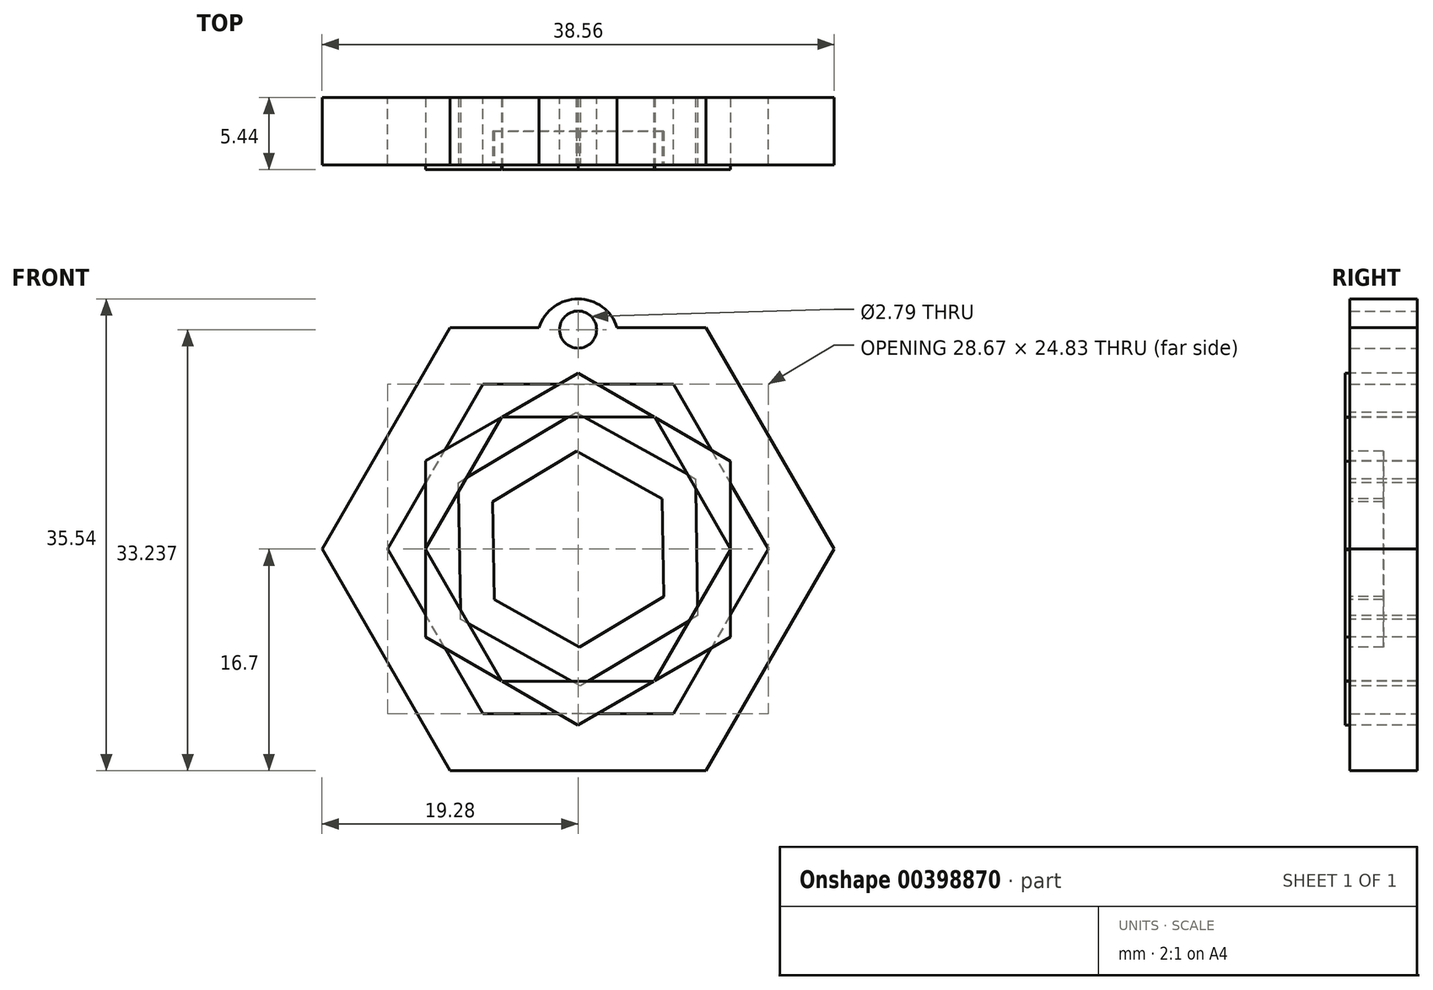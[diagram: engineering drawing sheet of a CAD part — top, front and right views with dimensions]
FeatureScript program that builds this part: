
annotation { "Feature Type Name" : "Feature", "Feature Type Description" : "" }
export const myFeature = defineFeature(function(context is Context, id is Id, definition is map)
    precondition{}
    {
        {
            var Q0;
            Q0=qCreatedBy(makeId("Front.planeOp"),FACE);
            var sketch = newSketch(context, id + "F0", { "sketchPlane" : qUnion([Q0])});
            skCircle(sketch, "E0.cCircle", {"center": v(0, 0) * mm, "radius": 16.7 * mm, "construction": true});
            skLineSegment(sketch, "E0.0", {"start": v(9.64, -16.7) * mm, "end": v(-9.64, -16.7) * mm});
            skLineSegment(sketch, "E0.1", {"start": v(-9.64, -16.7) * mm, "end": v(-19.28, 0) * mm});
            skLineSegment(sketch, "E0.2", {"start": v(-19.28, 0) * mm, "end": v(-9.64, 16.7) * mm});
            skLineSegment(sketch, "E0.3", {"start": v(-9.64, 16.7) * mm, "end": v(9.64, 16.7) * mm});
            skLineSegment(sketch, "E0.4", {"start": v(9.64, 16.7) * mm, "end": v(19.28, 0) * mm});
            skLineSegment(sketch, "E0.5", {"start": v(19.28, 0) * mm, "end": v(9.64, -16.7) * mm});
            skPoint(sketch, "E0.0.midPoint", {"position": v(0, -16.7) * mm});
            skCircle(sketch, "E1.cCircle", {"center": v(0, 0) * mm, "radius": 12.42 * mm, "construction": true});
            skLineSegment(sketch, "E1.0", {"start": v(7.17, -12.42) * mm, "end": v(-7.17, -12.42) * mm});
            skLineSegment(sketch, "E1.1", {"start": v(-7.17, -12.42) * mm, "end": v(-14.34, 0) * mm});
            skLineSegment(sketch, "E1.2", {"start": v(-14.34, 0) * mm, "end": v(-7.17, 12.42) * mm});
            skLineSegment(sketch, "E1.3", {"start": v(-7.17, 12.42) * mm, "end": v(7.17, 12.42) * mm});
            skLineSegment(sketch, "E1.4", {"start": v(7.17, 12.42) * mm, "end": v(14.34, 0) * mm});
            skLineSegment(sketch, "E1.5", {"start": v(14.34, 0) * mm, "end": v(7.17, -12.42) * mm});
            skPoint(sketch, "E1.0.midPoint", {"position": v(0, -12.42) * mm});
            skSolve(sketch);
        }
        {
            var Q0;
            Q0=makeQuery(id+"F0.imprint","IMPRINT",FACE,{"disambiguationData":[TD([[makeQuery(id+"F0.imprint","IMPRINT",EDGE,{"derivedFrom":sQuery(id+"F0.wireOp",EDGE,"E0.0")}),-1.0]])]});
            extrude(context, id + "F1", {"entities" : qUnion([Q0]), "depth" : 5.08 * mm});
        }
        {
            var Q0;
            Q0=qCreatedBy(makeId("Front.planeOp"),FACE);
            var sketch = newSketch(context, id + "F2", { "sketchPlane" : qUnion([Q0])});
            skCircle(sketch, "E2", {"center": v(0, 15.77) * mm, "radius": 3.08 * mm});
            skSolve(sketch);
        }
        {
            var Q0;
            Q0=makeQuery(id+"F2.imprint","IMPRINT",FACE,{"disambiguationData":[TD([[makeQuery(id+"F2.imprint","IMPRINT",EDGE,{"derivedFrom":sQuery(id+"F2.wireOp",EDGE,"E2")}),1.0]])]});
            extrude(context, id + "F3", {"entities" : qUnion([Q0]), "operationType" : NewBodyOperationType.ADD, "depth" : 5.08 * mm});
        }
        {
            var Q0;
            Q0=qCreatedBy(makeId("Front.planeOp"),FACE);
            var sketch = newSketch(context, id + "F4", { "sketchPlane" : qUnion([Q0])});
            skPoint(sketch, "E3", {"position": v(0, 16.54) * mm});
            skSolve(sketch);
        }
        {
            var Q0;
            Q0=sQuery(id+"F4.wireOp",VERTEX,"E3");
            var Q1;
            Q1=makeQuery(id+"F1.opExtrude","SWEPT_BODY",BODY,{"disambiguationData":[OSD([sQuery(id+"F0.wireOp",EDGE,"E0.0"),sQuery(id+"F0.wireOp",EDGE,"E0.1"),sQuery(id+"F0.wireOp",EDGE,"E0.2"),sQuery(id+"F0.wireOp",EDGE,"E0.3"),sQuery(id+"F0.wireOp",EDGE,"E0.4"),sQuery(id+"F0.wireOp",EDGE,"E0.5"),sQuery(id+"F0.wireOp",EDGE,"E1.0"),sQuery(id+"F0.wireOp",EDGE,"E1.1"),sQuery(id+"F0.wireOp",EDGE,"E1.2"),sQuery(id+"F0.wireOp",EDGE,"E1.3"),sQuery(id+"F0.wireOp",EDGE,"E1.4"),sQuery(id+"F0.wireOp",EDGE,"E1.5")])]});
            hole(context, id + "F5", {"style" : HoleStyle.SIMPLE, "endStyle" : HoleEndStyle.THROUGH, "oppositeDirection" : true, "holeDiameter" : 2.8 * mm, "isTappedThrough" : true, "tappedDepth" : 12.7 * mm, "tapClearance" : 3, "locations" : qUnion([Q0]), "scope" : qUnion([Q1])});
        }
        {
            var Q0;
            Q0=makeQuery(id+"F3.boolean.opBoolean","MERGE",FACE,{"derivedFrom":[makeQuery(id+"F1.opExtrude","CAP_FACE",FACE,{"disambiguationData":[OSD([sQuery(id+"F0.wireOp",EDGE,"E0.0"),sQuery(id+"F0.wireOp",EDGE,"E0.1"),sQuery(id+"F0.wireOp",EDGE,"E0.2"),sQuery(id+"F0.wireOp",EDGE,"E0.3"),sQuery(id+"F0.wireOp",EDGE,"E0.4"),sQuery(id+"F0.wireOp",EDGE,"E0.5"),sQuery(id+"F0.wireOp",EDGE,"E1.0"),sQuery(id+"F0.wireOp",EDGE,"E1.1"),sQuery(id+"F0.wireOp",EDGE,"E1.2"),sQuery(id+"F0.wireOp",EDGE,"E1.3"),sQuery(id+"F0.wireOp",EDGE,"E1.4"),sQuery(id+"F0.wireOp",EDGE,"E1.5")])],"isStart":false}),makeQuery(id+"F3.opExtrude","CAP_FACE",FACE,{"disambiguationData":[OSD([sQuery(id+"F2.wireOp",EDGE,"E2")])],"isStart":false})]});
            var sketch = newSketch(context, id + "F6", { "sketchPlane" : qUnion([Q0])});
            skCircle(sketch, "E4.cCircle", {"center": v(0, 0) * mm, "radius": 10.73 * mm, "construction": true});
            skLineSegment(sketch, "E4.0", {"start": v(0, 12.39) * mm, "end": v(10.73, 6.19) * mm});
            skLineSegment(sketch, "E4.1", {"start": v(10.73, 6.19) * mm, "end": v(10.72, -6.2) * mm});
            skLineSegment(sketch, "E4.2", {"start": v(10.72, -6.2) * mm, "end": v(0, -12.39) * mm});
            skLineSegment(sketch, "E4.3", {"start": v(0, -12.39) * mm, "end": v(-10.73, -6.19) * mm});
            skLineSegment(sketch, "E4.4", {"start": v(-10.73, -6.19) * mm, "end": v(-10.72, 6.2) * mm});
            skLineSegment(sketch, "E4.5", {"start": v(-10.72, 6.2) * mm, "end": v(0, 12.39) * mm});
            skPoint(sketch, "E4.0.midPoint", {"position": v(5.37, 9.29) * mm});
            skCircle(sketch, "E5.cCircle", {"center": v(0, 0) * mm, "radius": 9.3 * mm, "construction": true});
            skLineSegment(sketch, "E5.0", {"start": v(5.38, 9.3) * mm, "end": v(10.75, 0) * mm});
            skLineSegment(sketch, "E5.1", {"start": v(10.75, 0) * mm, "end": v(5.37, -9.31) * mm});
            skLineSegment(sketch, "E5.2", {"start": v(5.37, -9.31) * mm, "end": v(-5.38, -9.3) * mm});
            skLineSegment(sketch, "E5.3", {"start": v(-5.38, -9.3) * mm, "end": v(-10.75, 0) * mm});
            skLineSegment(sketch, "E5.4", {"start": v(-10.75, 0) * mm, "end": v(-5.37, 9.31) * mm});
            skLineSegment(sketch, "E5.5", {"start": v(-5.37, 9.31) * mm, "end": v(5.38, 9.3) * mm});
            skPoint(sketch, "E5.0.midPoint", {"position": v(8.06, 4.65) * mm});
            skCircle(sketch, "E6.cCircle", {"center": v(0, 0) * mm, "radius": 8.04 * mm, "construction": true});
            skLineSegment(sketch, "E6.0", {"start": v(-8.04, 4.65) * mm, "end": v(0, 9.28) * mm});
            skLineSegment(sketch, "E6.1", {"start": v(0, 9.28) * mm, "end": v(8.04, 4.64) * mm});
            skLineSegment(sketch, "E6.2", {"start": v(8.04, 4.64) * mm, "end": v(8.04, -4.65) * mm});
            skLineSegment(sketch, "E6.3", {"start": v(8.04, -4.65) * mm, "end": v(0, -9.28) * mm});
            skLineSegment(sketch, "E6.4", {"start": v(0, -9.28) * mm, "end": v(-8.04, -4.64) * mm});
            skLineSegment(sketch, "E6.5", {"start": v(-8.04, -4.64) * mm, "end": v(-8.04, 4.65) * mm});
            skPoint(sketch, "E6.0.midPoint", {"position": v(-4.01, 6.97) * mm});
            skCircle(sketch, "E7.cCircle", {"center": v(0, 0) * mm, "radius": 6.97 * mm, "construction": true});
            skLineSegment(sketch, "E7.0", {"start": v(-4.02, 6.97) * mm, "end": v(4.02, 6.97) * mm});
            skLineSegment(sketch, "E7.1", {"start": v(4.02, 6.97) * mm, "end": v(8.04, 0) * mm});
            skLineSegment(sketch, "E7.2", {"start": v(8.04, 0) * mm, "end": v(4.02, -6.97) * mm});
            skLineSegment(sketch, "E7.3", {"start": v(4.02, -6.97) * mm, "end": v(-4.02, -6.97) * mm});
            skLineSegment(sketch, "E7.4", {"start": v(-4.02, -6.97) * mm, "end": v(-8.04, 0) * mm});
            skLineSegment(sketch, "E7.5", {"start": v(-8.04, 0) * mm, "end": v(-4.02, 6.97) * mm});
            skPoint(sketch, "E7.0.midPoint", {"position": v(0, 6.97) * mm});
            skSolve(sketch);
        }
        {
            var Q0;
            {var subQ0=sQuery(id+"F6.wireOp",EDGE,"E4.5");var subQ1=sQuery(id+"F6.wireOp",EDGE,"E4.0");var subQ2=makeQuery(id+"F6.imprint","INTERSECT",VERTEX,{"derivedFrom":[subQ1,subQ0]});Q0=makeQuery(id+"F6.imprint","IMPRINT",FACE,{"disambiguationData":[TD([[makeQuery(id+"F6.imprint","IMPRINT",EDGE,{"disambiguationData":[TD([[subQ2,-1.0]])],"derivedFrom":subQ1}),-1.0]])]});}
            var Q1;
            {var subQ0=sQuery(id+"F6.wireOp",EDGE,"E4.5");var subQ1=sQuery(id+"F6.wireOp",EDGE,"E4.4");var subQ2=makeQuery(id+"F6.imprint","INTERSECT",VERTEX,{"derivedFrom":[subQ1,subQ0]});Q1=makeQuery(id+"F6.imprint","IMPRINT",FACE,{"disambiguationData":[TD([[makeQuery(id+"F6.imprint","IMPRINT",EDGE,{"disambiguationData":[TD([[subQ2,1.0]])],"derivedFrom":subQ1}),-1.0]])]});}
            var Q2;
            {var subQ0=sQuery(id+"F6.wireOp",EDGE,"E4.4");var subQ1=sQuery(id+"F6.wireOp",EDGE,"E4.3");var subQ2=makeQuery(id+"F6.imprint","INTERSECT",VERTEX,{"derivedFrom":[subQ1,subQ0]});Q2=makeQuery(id+"F6.imprint","IMPRINT",FACE,{"disambiguationData":[TD([[makeQuery(id+"F6.imprint","IMPRINT",EDGE,{"disambiguationData":[TD([[subQ2,1.0]])],"derivedFrom":subQ1}),-1.0]])]});}
            var Q3;
            {var subQ14=sQuery(id+"F6.wireOp",EDGE,"E6.0");var subQ20=sQuery(id+"F6.wireOp",EDGE,"E7.5");var subQ23=makeQuery(id+"F6.imprint","INTERSECT",VERTEX,{"derivedFrom":[subQ14,subQ20]});Q3=makeQuery(id+"F6.imprint","IMPRINT",FACE,{"disambiguationData":[TD([[makeQuery(id+"F6.imprint","IMPRINT",EDGE,{"disambiguationData":[TD([[subQ23,-1.0]])],"derivedFrom":subQ14}),-1.0]])]});}
            var Q4;
            {var subQ0=sQuery(id+"F6.wireOp",EDGE,"E4.1");var subQ1=sQuery(id+"F6.wireOp",EDGE,"E4.0");var subQ2=makeQuery(id+"F6.imprint","INTERSECT",VERTEX,{"derivedFrom":[subQ1,subQ0]});Q4=makeQuery(id+"F6.imprint","IMPRINT",FACE,{"disambiguationData":[TD([[makeQuery(id+"F6.imprint","IMPRINT",EDGE,{"disambiguationData":[TD([[subQ2,1.0]])],"derivedFrom":subQ1}),-1.0]])]});}
            var Q5;
            {var subQ0=sQuery(id+"F6.wireOp",EDGE,"E4.2");var subQ1=sQuery(id+"F6.wireOp",EDGE,"E4.1");var subQ2=makeQuery(id+"F6.imprint","INTERSECT",VERTEX,{"derivedFrom":[subQ1,subQ0]});Q5=makeQuery(id+"F6.imprint","IMPRINT",FACE,{"disambiguationData":[TD([[makeQuery(id+"F6.imprint","IMPRINT",EDGE,{"disambiguationData":[TD([[subQ2,1.0]])],"derivedFrom":subQ1}),-1.0]])]});}
            var Q6;
            {var subQ0=sQuery(id+"F6.wireOp",EDGE,"E4.3");var subQ1=sQuery(id+"F6.wireOp",EDGE,"E4.2");var subQ2=makeQuery(id+"F6.imprint","INTERSECT",VERTEX,{"derivedFrom":[subQ1,subQ0]});Q6=makeQuery(id+"F6.imprint","IMPRINT",FACE,{"disambiguationData":[TD([[makeQuery(id+"F6.imprint","IMPRINT",EDGE,{"disambiguationData":[TD([[subQ2,1.0]])],"derivedFrom":subQ1}),-1.0]])]});}
            extrude(context, id + "F7", {"entities" : qUnion([Q0, Q1, Q2, Q3, Q4, Q5, Q6]), "oppositeDirection" : true, "depth" : 5.08 * mm});
        }
        {
            var Q0;
            Q0=makeQuery(id+"F7.opExtrude","SWEPT_BODY",BODY,{"disambiguationData":[OSD([sQuery(id+"F6.wireOp",EDGE,"E4.0"),sQuery(id+"F6.wireOp",EDGE,"E4.1"),sQuery(id+"F6.wireOp",EDGE,"E5.0")])]});
            var Q1;
            Q1=makeQuery(id+"F7.opExtrude","SWEPT_BODY",BODY,{"disambiguationData":[OSD([sQuery(id+"F6.wireOp",EDGE,"E4.1"),sQuery(id+"F6.wireOp",EDGE,"E4.2"),sQuery(id+"F6.wireOp",EDGE,"E5.1")])]});
            var Q2;
            Q2=makeQuery(id+"F7.opExtrude","SWEPT_BODY",BODY,{"disambiguationData":[OSD([sQuery(id+"F6.wireOp",EDGE,"E4.2"),sQuery(id+"F6.wireOp",EDGE,"E4.3"),sQuery(id+"F6.wireOp",EDGE,"E5.2")])]});
            var Q3;
            Q3=makeQuery(id+"F7.opExtrude","SWEPT_BODY",BODY,{"disambiguationData":[OSD([sQuery(id+"F6.wireOp",EDGE,"E4.3"),sQuery(id+"F6.wireOp",EDGE,"E4.4"),sQuery(id+"F6.wireOp",EDGE,"E5.3")])]});
            var Q4;
            Q4=makeQuery(id+"F7.opExtrude","SWEPT_BODY",BODY,{"disambiguationData":[OSD([sQuery(id+"F6.wireOp",EDGE,"E4.4"),sQuery(id+"F6.wireOp",EDGE,"E4.5"),sQuery(id+"F6.wireOp",EDGE,"E5.4")])]});
            var Q5;
            Q5=makeQuery(id+"F7.opExtrude","SWEPT_BODY",BODY,{"disambiguationData":[OSD([sQuery(id+"F6.wireOp",EDGE,"E4.0"),sQuery(id+"F6.wireOp",EDGE,"E4.5"),sQuery(id+"F6.wireOp",EDGE,"E5.5")])]});
            var Q6;
            Q6=qCreatedBy(makeId("Origin.pointOp"),VERTEX);
            transform(context, id + "F8", {"entities" : qUnion([Q0, Q1, Q2, Q3, Q4, Q5]), "transformType" : TransformType.SCALE_UNIFORMLY, "scale" : 1.07, "scalePoint" : qUnion([Q6]), "makeCopy" : false});
        }
        {
            var Q0;
            Q0=makeQuery(id+"F7.opExtrude","CAP_FACE",FACE,{"disambiguationData":[OSD([sQuery(id+"F6.wireOp",EDGE,"E6.0"),sQuery(id+"F6.wireOp",EDGE,"E6.1"),sQuery(id+"F6.wireOp",EDGE,"E6.2"),sQuery(id+"F6.wireOp",EDGE,"E6.3"),sQuery(id+"F6.wireOp",EDGE,"E6.4"),sQuery(id+"F6.wireOp",EDGE,"E6.5"),sQuery(id+"F6.wireOp",EDGE,"E7.0"),sQuery(id+"F6.wireOp",EDGE,"E7.1"),sQuery(id+"F6.wireOp",EDGE,"E7.2"),sQuery(id+"F6.wireOp",EDGE,"E7.3"),sQuery(id+"F6.wireOp",EDGE,"E7.4"),sQuery(id+"F6.wireOp",EDGE,"E7.5")])],"isStart":true});
            var sketch = newSketch(context, id + "F9", { "sketchPlane" : qUnion([Q0])});
            skPoint(sketch, "E8", {"position": v(0, 0) * mm});
            skCircle(sketch, "E9.cCircle", {"center": v(0, 0) * mm, "radius": 8.93 * mm, "construction": true});
            skLineSegment(sketch, "E9.0", {"start": v(9, -5) * mm, "end": v(0.17, -10.3) * mm});
            skLineSegment(sketch, "E9.1", {"start": v(0.17, -10.3) * mm, "end": v(-8.84, -5.3) * mm});
            skLineSegment(sketch, "E9.2", {"start": v(-8.84, -5.3) * mm, "end": v(-9, 5) * mm});
            skLineSegment(sketch, "E9.3", {"start": v(-9, 5) * mm, "end": v(-0.17, 10.3) * mm});
            skLineSegment(sketch, "E9.4", {"start": v(-0.17, 10.3) * mm, "end": v(8.84, 5.3) * mm});
            skLineSegment(sketch, "E9.5", {"start": v(8.84, 5.3) * mm, "end": v(9, -5) * mm});
            skPoint(sketch, "E9.0.midPoint", {"position": v(4.59, -7.66) * mm});
            skSolve(sketch);
        }
        {
            var Q0;
            Q0 = qSketchRegion(id + "F9", true);
            extrude(context, id + "F10", {"entities" : qUnion([Q0]), "oppositeDirection" : true, "depth" : 5.08 * mm});
        }
        {
            var Q0;
            Q0=makeQuery(id+"F7.opExtrude","CAP_FACE",FACE,{"disambiguationData":[OSD([sQuery(id+"F6.wireOp",EDGE,"E6.0"),sQuery(id+"F6.wireOp",EDGE,"E6.1"),sQuery(id+"F6.wireOp",EDGE,"E6.2"),sQuery(id+"F6.wireOp",EDGE,"E6.3"),sQuery(id+"F6.wireOp",EDGE,"E6.4"),sQuery(id+"F6.wireOp",EDGE,"E6.5"),sQuery(id+"F6.wireOp",EDGE,"E7.0"),sQuery(id+"F6.wireOp",EDGE,"E7.1"),sQuery(id+"F6.wireOp",EDGE,"E7.2"),sQuery(id+"F6.wireOp",EDGE,"E7.3"),sQuery(id+"F6.wireOp",EDGE,"E7.4"),sQuery(id+"F6.wireOp",EDGE,"E7.5")])],"isStart":true});
            extrude(context, id + "F11", {"entities" : qUnion([Q0]), "oppositeDirection" : true, "depth" : 1.5 * mm});
        }
        {
            var Q0;
            Q0=makeQuery(id+"F7.opExtrude","SWEPT_BODY",BODY,{"disambiguationData":[OSD([sQuery(id+"F6.wireOp",EDGE,"E6.0"),sQuery(id+"F6.wireOp",EDGE,"E6.1"),sQuery(id+"F6.wireOp",EDGE,"E6.2"),sQuery(id+"F6.wireOp",EDGE,"E6.3"),sQuery(id+"F6.wireOp",EDGE,"E6.4"),sQuery(id+"F6.wireOp",EDGE,"E6.5"),sQuery(id+"F6.wireOp",EDGE,"E7.0"),sQuery(id+"F6.wireOp",EDGE,"E7.1"),sQuery(id+"F6.wireOp",EDGE,"E7.2"),sQuery(id+"F6.wireOp",EDGE,"E7.3"),sQuery(id+"F6.wireOp",EDGE,"E7.4"),sQuery(id+"F6.wireOp",EDGE,"E7.5")])]});
            deleteBodies(context, id + "F12", {"entities" : qUnion([Q0])});
        }
        {
            var Q0;
            Q0=makeQuery(id+"F11.opExtrude","SWEPT_BODY",BODY,{"disambiguationData":[OSD([sQuery(id+"F6.wireOp",EDGE,"E6.0"),sQuery(id+"F6.wireOp",EDGE,"E6.1"),sQuery(id+"F6.wireOp",EDGE,"E6.2"),sQuery(id+"F6.wireOp",EDGE,"E6.3"),sQuery(id+"F6.wireOp",EDGE,"E6.4"),sQuery(id+"F6.wireOp",EDGE,"E6.5"),sQuery(id+"F6.wireOp",EDGE,"E7.0"),sQuery(id+"F6.wireOp",EDGE,"E7.1"),sQuery(id+"F6.wireOp",EDGE,"E7.2"),sQuery(id+"F6.wireOp",EDGE,"E7.3"),sQuery(id+"F6.wireOp",EDGE,"E7.4"),sQuery(id+"F6.wireOp",EDGE,"E7.5")])]});
            deleteBodies(context, id + "F13", {"entities" : qUnion([Q0])});
        }
        {
            var Q0;
            Q0=makeQuery(id+"F10.opExtrude","CAP_FACE",FACE,{"disambiguationData":[OSD([sQuery(id+"F9.wireOp",EDGE,"E9.0"),sQuery(id+"F9.wireOp",EDGE,"E9.1"),sQuery(id+"F9.wireOp",EDGE,"E9.2"),sQuery(id+"F9.wireOp",EDGE,"E9.3"),sQuery(id+"F9.wireOp",EDGE,"E9.4"),sQuery(id+"F9.wireOp",EDGE,"E9.5")])],"isStart":true});
            shell(context, id + "F14", {"entities" : qUnion([Q0]), "thickness" : 2.54 * mm});
        }
    });
